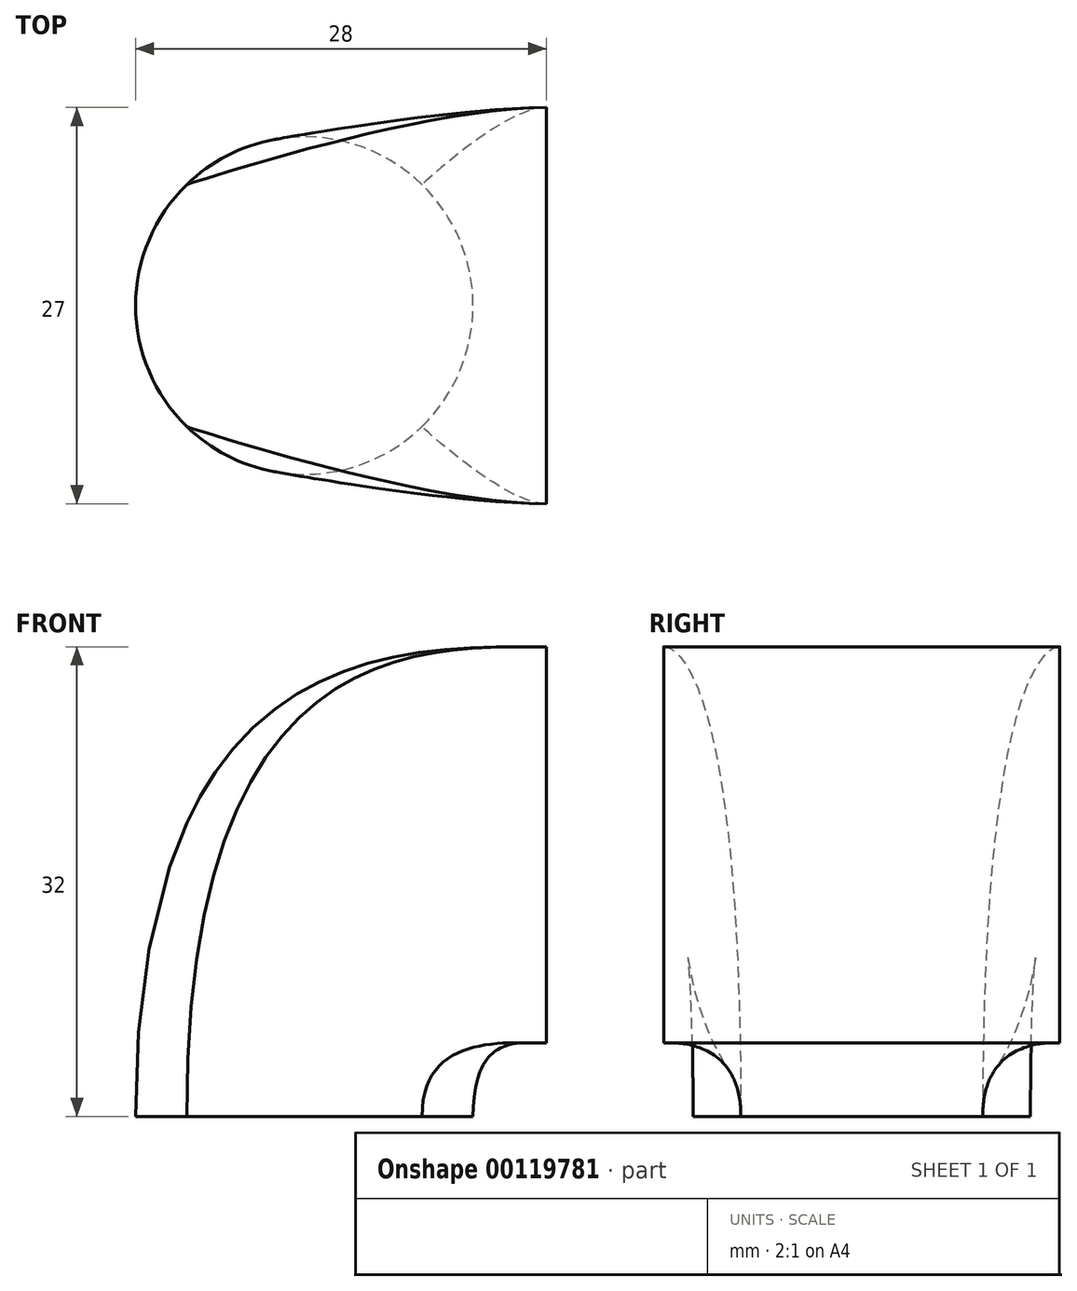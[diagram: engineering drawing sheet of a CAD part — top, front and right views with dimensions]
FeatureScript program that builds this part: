
annotation { "Feature Type Name" : "Feature", "Feature Type Description" : "" }
export const myFeature = defineFeature(function(context is Context, id is Id, definition is map)
    precondition{}
    {
        {
            var Q0;
            Q0=qCreatedBy(makeId("Top.planeOp"),FACE);
            var sketch = newSketch(context, id + "F0", { "sketchPlane" : qUnion([Q0])});
            skLineSegment(sketch, "E0.bottom", {"start": v(-24.52, 8.24) * mm, "end": v(-8.48, 8.24) * mm, "construction": true});
            skLineSegment(sketch, "E0.top", {"start": v(-24.52, -8.24) * mm, "end": v(-8.48, -8.24) * mm, "construction": true});
            skLineSegment(sketch, "E0.left", {"start": v(-24.52, 8.24) * mm, "end": v(-24.52, -8.24) * mm, "construction": true});
            skLineSegment(sketch, "E0.right", {"start": v(-8.48, 8.24) * mm, "end": v(-8.48, -8.24) * mm, "construction": true});
            skArc(sketch, "E1", {"start": v(-8.48, 8.24) * mm, "mid": v(-16.5, 11.5) * mm, "end": v(-24.52, 8.24) * mm});
            skArc(sketch, "E2", {"start": v(-24.52, 8.24) * mm, "mid": v(-28, 0) * mm, "end": v(-24.52, -8.24) * mm});
            skArc(sketch, "E3", {"start": v(-24.52, -8.24) * mm, "mid": v(-16.5, -11.5) * mm, "end": v(-8.48, -8.24) * mm});
            skArc(sketch, "E4", {"start": v(-8.48, -8.24) * mm, "mid": v(-5, 0) * mm, "end": v(-8.48, 8.24) * mm});
            skSolve(sketch);
        }
        {
            var Q0;
            Q0=qCreatedBy(makeId("Right.planeOp"),FACE);
            var sketch = newSketch(context, id + "F1", { "sketchPlane" : qUnion([Q0])});
            skLineSegment(sketch, "E5.bottom", {"start": v(13.5, 5) * mm, "end": v(-13.5, 5) * mm});
            skLineSegment(sketch, "E5.top", {"start": v(13.5, 32) * mm, "end": v(-13.5, 32) * mm});
            skLineSegment(sketch, "E5.left", {"start": v(13.5, 5) * mm, "end": v(13.5, 32) * mm});
            skLineSegment(sketch, "E5.right", {"start": v(-13.5, 5) * mm, "end": v(-13.5, 32) * mm});
            skPoint(sketch, "E5.middle", {"position": v(0, 18.5) * mm});
            skSolve(sketch);
        }
        {
            var Q0;
            Q0=makeQuery(id+"F1.imprint","IMPRINT",FACE,{"disambiguationData":[TD([[makeQuery(id+"F1.imprint","IMPRINT",EDGE,{"derivedFrom":sQuery(id+"F1.wireOp",EDGE,"E5.bottom")}),-1.0]])]});
            var Q1;
            Q1=makeQuery(id+"F0.imprint","IMPRINT",FACE,{"disambiguationData":[TD([[makeQuery(id+"F0.imprint","IMPRINT",EDGE,{"derivedFrom":sQuery(id+"F0.wireOp",EDGE,"E1")}),1.0]])]});
            loft(context, id + "F2", {"startCondition" : LoftEndDerivativeType.NORMAL_TO_PROFILE, "startMagnitude" : 1, "endCondition" : LoftEndDerivativeType.NORMAL_TO_PROFILE, "endMagnitude" : 3, "sheetProfilesArray" : [{ "sheetProfileEntities" : qUnion([Q0]) }, { "sheetProfileEntities" : qUnion([Q1]) }]});
        }
    });
